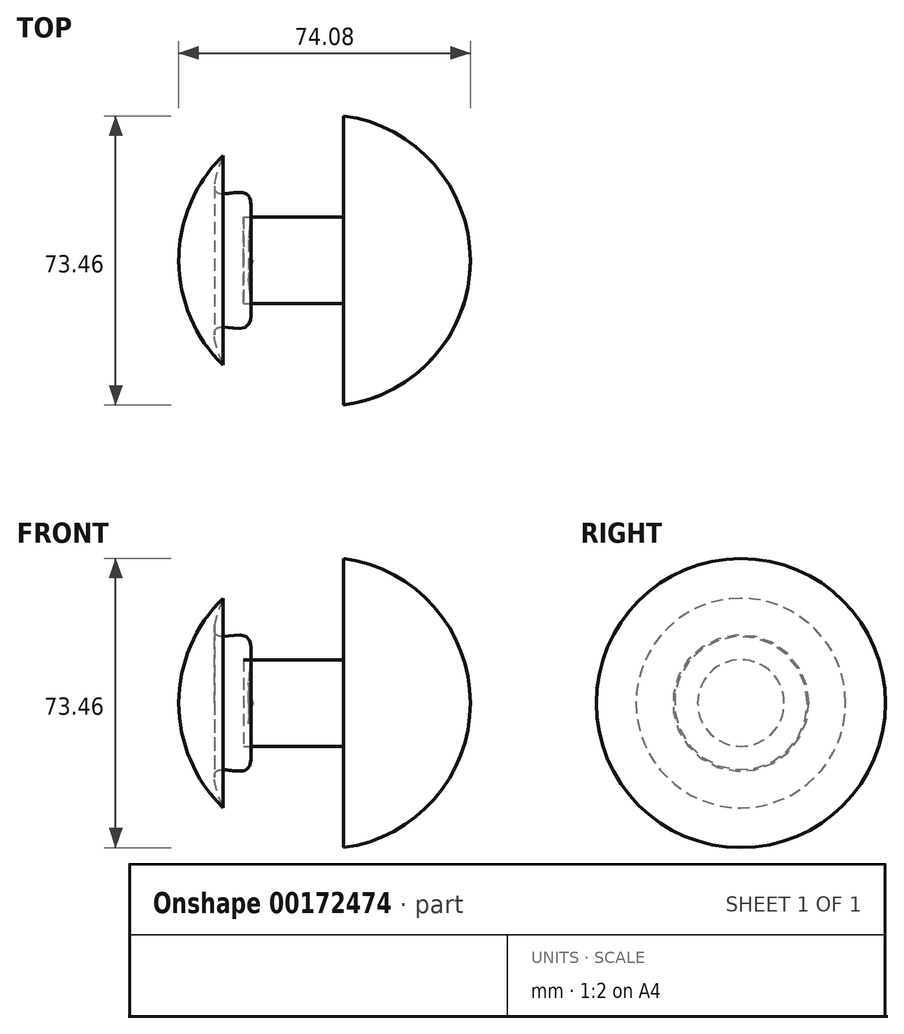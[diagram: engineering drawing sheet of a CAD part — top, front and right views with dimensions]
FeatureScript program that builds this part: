
annotation { "Feature Type Name" : "Feature", "Feature Type Description" : "" }
export const myFeature = defineFeature(function(context is Context, id is Id, definition is map)
    precondition{}
    {
        {
            var Q0;
            Q0=qCreatedBy(makeId("Top.planeOp"),FACE);
            var sketch = newSketch(context, id + "F0", { "sketchPlane" : qUnion([Q0])});
            skArc(sketch, "E0", {"start": v(37.04, 0) * mm, "mid": v(27.85, 24.43) * mm, "end": v(4.83, 36.73) * mm});
            skLineSegment(sketch, "E1", {"start": v(-37.04, 0) * mm, "end": v(37.04, 0) * mm});
            skArc(sketch, "E2.0", {"start": v(43.4, 0) * mm, "mid": v(32.34, 28.92) * mm, "end": v(4.83, 43.12) * mm});
            skLineSegment(sketch, "E3", {"start": v(-3.84, 43.22) * mm, "end": v(-3.84, 0) * mm});
            skLineSegment(sketch, "E4", {"start": v(-3.84, 0) * mm, "end": v(4.83, 0) * mm});
            skLineSegment(sketch, "E5", {"start": v(4.83, 0) * mm, "end": v(4.83, 43.12) * mm});
            skArc(sketch, "E6.trimOffspring", {"start": v(-3.84, 43.22) * mm, "mid": v(-32.01, 29.3) * mm, "end": v(-43.4, 0) * mm});
            skArc(sketch, "E7.trimOffspring", {"start": v(-3.84, 36.84) * mm, "mid": v(-27.52, 24.8) * mm, "end": v(-37.04, 0) * mm});
            skFitSpline(sketch, "E8", {"points": [v(-25.76, 26.62) * mm, v(-27.25, 17.18) * mm, v(-19.79, 16.84) * mm, v(-19.26, 5.73) * mm, v(-18.05, 0) * mm], "startDerivative": vector(-18.3, -47.58) * mm, "endDerivative": vector(9.3, -21.84) * mm});
            skSolve(sketch);
        }
        {
            var Q0;
            {var subQ0=sQuery(id+"F0.wireOp",EDGE,"E7.trimOffspring");Q0=makeQuery(id+"F0.imprint","IMPRINT",FACE,{"disambiguationData":[TD([[makeQuery(id+"F0.imprint","IMPRINT",EDGE,{"derivedFrom":subQ0}),1.0]])]});}
            var Q1;
            {var subQ0=sQuery(id+"F0.wireOp",EDGE,"E0");Q1=makeQuery(id+"F0.imprint","IMPRINT",FACE,{"disambiguationData":[TD([[makeQuery(id+"F0.imprint","IMPRINT",EDGE,{"derivedFrom":subQ0}),1.0]])]});}
            var Q2;
            Q2=sQuery(id+"F0.wireOp",EDGE,"E1");
            revolve(context, id + "F1", {"entities" : qUnion([Q0, Q1]), "axis" : qUnion([Q2]), "revolveType" : RevolveType.FULL});
        }
        {
            var Q0;
            Q0=makeQuery(id+"F1.opRevolve","SWEPT_FACE",FACE,{"disambiguationData":[OSD([sQuery(id+"F0.wireOp",EDGE,"E5")])]});
            var sketch = newSketch(context, id + "F2", { "sketchPlane" : qUnion([Q0])});
            skCircle(sketch, "E9", {"center": v(0, 0) * mm, "radius": 11 * mm});
            skSolve(sketch);
        }
        {
            var Q0;
            Q0 = qSketchRegion(id + "F2", true);
            extrude(context, id + "F3", {"entities" : qUnion([Q0]), "depth" : 25.4 * mm});
        }
    });
